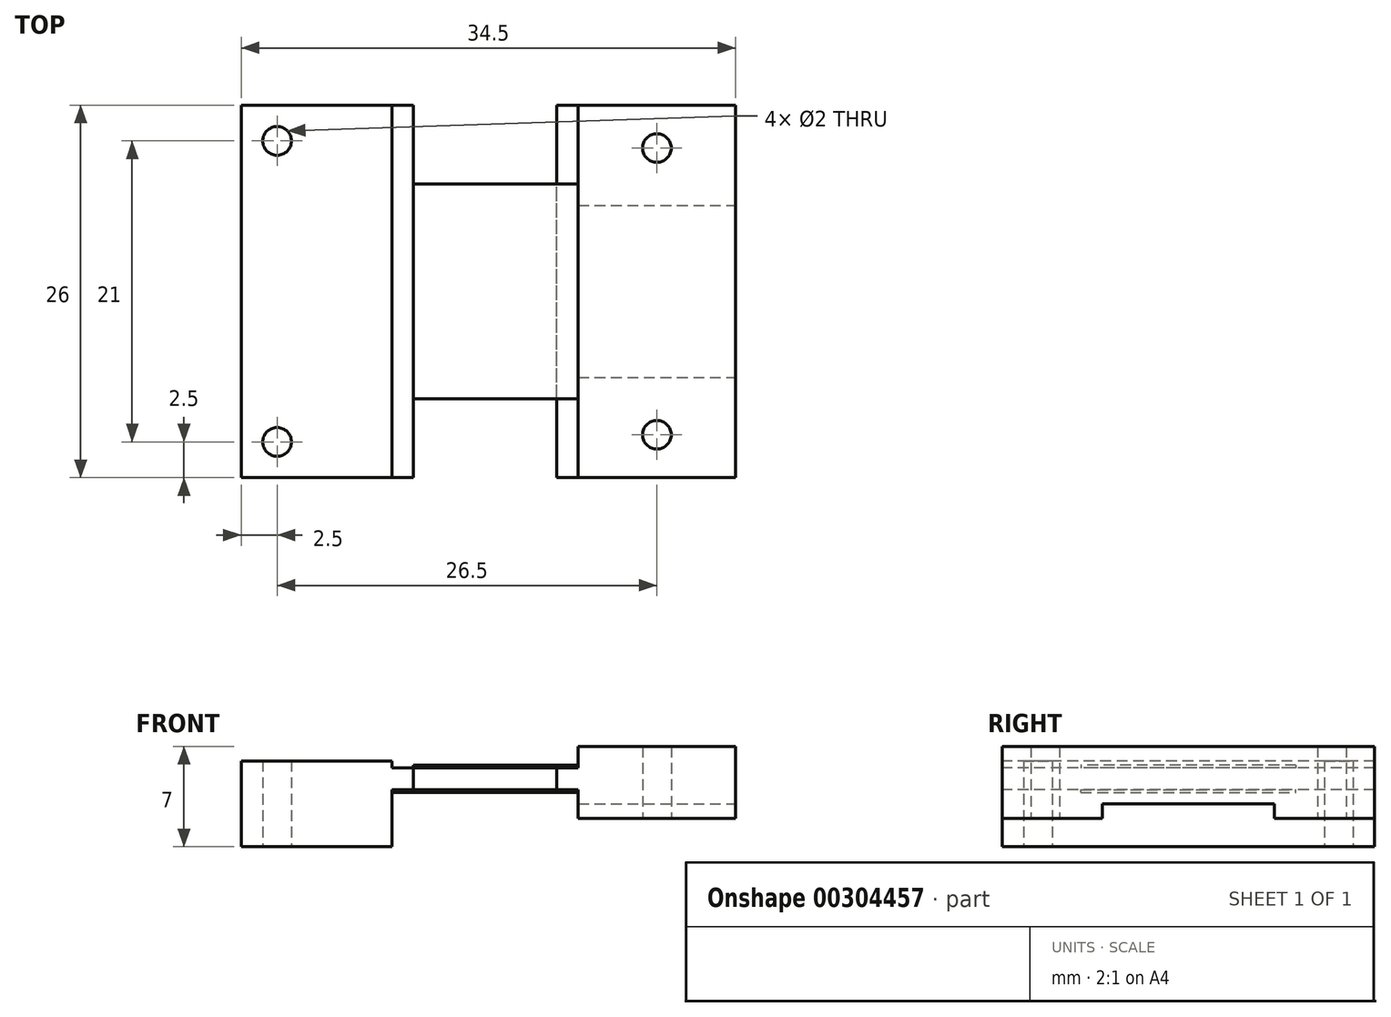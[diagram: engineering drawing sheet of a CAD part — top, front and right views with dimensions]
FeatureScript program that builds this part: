
annotation { "Feature Type Name" : "Feature", "Feature Type Description" : "" }
export const myFeature = defineFeature(function(context is Context, id is Id, definition is map)
    precondition{}
    {
        {
            var Q0;
            Q0=qCreatedBy(makeId("Top.planeOp"),FACE);
            var sketch = newSketch(context, id + "F0", { "sketchPlane" : qUnion([Q0])});
            skLineSegment(sketch, "E0.bottom", {"start": v(6.25, -13) * mm, "end": v(-6.25, -13) * mm});
            skLineSegment(sketch, "E0.top", {"start": v(6.25, 13) * mm, "end": v(-6.25, 13) * mm});
            skLineSegment(sketch, "E0.left", {"start": v(6.25, -13) * mm, "end": v(6.25, 13) * mm});
            skLineSegment(sketch, "E0.right", {"start": v(-6.25, -13) * mm, "end": v(-6.25, 13) * mm});
            skPoint(sketch, "E0.middle", {"position": v(0, 0) * mm});
            skSolve(sketch);
        }
        {
            var Q0;
            Q0 = qSketchRegion(id + "F0", true);
            extrude(context, id + "F1", {"entities" : qUnion([Q0]), "depth" : 5 * mm});
        }
        {
            var Q0;
            Q0=makeQuery(id+"F1.opExtrude","CAP_FACE",FACE,{"disambiguationData":[OSD([sQuery(id+"F0.wireOp",EDGE,"E0.bottom"),sQuery(id+"F0.wireOp",EDGE,"E0.top"),sQuery(id+"F0.wireOp",EDGE,"E0.left"),sQuery(id+"F0.wireOp",EDGE,"E0.right")])],"isStart":false});
            var sketch = newSketch(context, id + "F2", { "sketchPlane" : qUnion([Q0])});
            skLineSegment(sketch, "E1.bottom", {"start": v(-6.25, 13) * mm, "end": v(-4.75, 13) * mm});
            skLineSegment(sketch, "E1.top", {"start": v(-6.25, -13) * mm, "end": v(-4.75, -13) * mm});
            skLineSegment(sketch, "E1.left", {"start": v(-6.25, 13) * mm, "end": v(-6.25, -13) * mm});
            skLineSegment(sketch, "E1.right", {"start": v(-4.75, 13) * mm, "end": v(-4.75, -13) * mm});
            skSolve(sketch);
        }
        {
            var Q0;
            Q0 = qSketchRegion(id + "F2", true);
            extrude(context, id + "F3", {"entities" : qUnion([Q0]), "operationType" : NewBodyOperationType.REMOVE, "oppositeDirection" : true, "depth" : 1.5 * mm});
        }
        {
            var Q0;
            Q0=makeQuery(id+"F1.opExtrude","CAP_FACE",FACE,{"disambiguationData":[OSD([sQuery(id+"F0.wireOp",EDGE,"E0.bottom"),sQuery(id+"F0.wireOp",EDGE,"E0.top"),sQuery(id+"F0.wireOp",EDGE,"E0.left"),sQuery(id+"F0.wireOp",EDGE,"E0.right")])],"isStart":true});
            var sketch = newSketch(context, id + "F4", { "sketchPlane" : qUnion([Q0])});
            skLineSegment(sketch, "E2.bottom", {"start": v(-6.25, 13) * mm, "end": v(-4.75, 13) * mm});
            skLineSegment(sketch, "E2.top", {"start": v(-6.25, -13) * mm, "end": v(-4.75, -13) * mm});
            skLineSegment(sketch, "E2.left", {"start": v(-6.25, 13) * mm, "end": v(-6.25, -13) * mm});
            skLineSegment(sketch, "E2.right", {"start": v(-4.75, 13) * mm, "end": v(-4.75, -13) * mm});
            skSolve(sketch);
        }
        {
            var Q0;
            Q0 = qSketchRegion(id + "F4", true);
            extrude(context, id + "F5", {"entities" : qUnion([Q0]), "operationType" : NewBodyOperationType.REMOVE, "oppositeDirection" : true, "depth" : 2 * mm});
        }
        {
            var Q0;
            Q0=makeQuery(id+"F1.opExtrude","CAP_FACE",FACE,{"disambiguationData":[OSD([sQuery(id+"F0.wireOp",EDGE,"E0.bottom"),sQuery(id+"F0.wireOp",EDGE,"E0.top"),sQuery(id+"F0.wireOp",EDGE,"E0.left"),sQuery(id+"F0.wireOp",EDGE,"E0.right")])],"isStart":true});
            var sketch = newSketch(context, id + "F6", { "sketchPlane" : qUnion([Q0])});
            skLineSegment(sketch, "E3.bottom", {"start": v(-4.75, 6) * mm, "end": v(6.25, 6) * mm});
            skLineSegment(sketch, "E3.top", {"start": v(-4.75, -6) * mm, "end": v(6.25, -6) * mm});
            skLineSegment(sketch, "E3.left", {"start": v(-4.75, 6) * mm, "end": v(-4.75, -6) * mm});
            skLineSegment(sketch, "E3.right", {"start": v(6.25, 6) * mm, "end": v(6.25, -6) * mm});
            skSolve(sketch);
        }
        {
            var Q0;
            Q0 = qSketchRegion(id + "F6", true);
            extrude(context, id + "F7", {"entities" : qUnion([Q0]), "operationType" : NewBodyOperationType.REMOVE, "oppositeDirection" : true, "depth" : 1 * mm});
        }
        {
            var Q0;
            Q0=makeQuery(id+"F1.opExtrude","CAP_FACE",FACE,{"disambiguationData":[OSD([sQuery(id+"F0.wireOp",EDGE,"E0.bottom"),sQuery(id+"F0.wireOp",EDGE,"E0.top"),sQuery(id+"F0.wireOp",EDGE,"E0.left"),sQuery(id+"F0.wireOp",EDGE,"E0.right")])],"isStart":false});
            var sketch = newSketch(context, id + "F8", { "sketchPlane" : qUnion([Q0])});
            skPoint(sketch, "E4", {"position": v(0.75, 10) * mm});
            skPoint(sketch, "E5", {"position": v(0.75, -10) * mm});
            skLineSegment(sketch, "E6", {"start": v(0.75, 16.57) * mm, "end": v(0.75, -16.02) * mm, "construction": true});
            skSolve(sketch);
        }
        {
            var Q0;
            Q0=sQuery(id+"F8.wireOp",VERTEX,"E4");
            var Q1;
            Q1=sQuery(id+"F8.wireOp",VERTEX,"E5");
            var Q2;
            Q2=makeQuery(id+"F1.opExtrude","SWEPT_BODY",BODY,{"disambiguationData":[OSD([sQuery(id+"F0.wireOp",EDGE,"E0.bottom"),sQuery(id+"F0.wireOp",EDGE,"E0.top"),sQuery(id+"F0.wireOp",EDGE,"E0.left"),sQuery(id+"F0.wireOp",EDGE,"E0.right")])]});
            hole(context, id + "F9", {"style" : HoleStyle.SIMPLE, "endStyle" : HoleEndStyle.BLIND, "holeDiameter" : 2 * mm, "holeDepth" : 10 * mm, "isTappedThrough" : true, "tappedDepth" : 12 * mm, "tapClearance" : 3, "locations" : qUnion([Q0, Q1]), "scope" : qUnion([Q2]), "startStyle" : HoleStartStyle.PART});
        }
        {
            var Q0;
            Q0=makeQuery(id+"F3.boolean.opBoolean","COPY",FACE,{"derivedFrom":makeQuery(id+"F3.opExtrude","CAP_FACE",FACE,{"disambiguationData":[OSD([sQuery(id+"F2.wireOp",EDGE,"E1.bottom"),sQuery(id+"F2.wireOp",EDGE,"E1.top"),sQuery(id+"F2.wireOp",EDGE,"E1.left"),sQuery(id+"F2.wireOp",EDGE,"E1.right")])],"isStart":false})});
            var sketch = newSketch(context, id + "F10", { "sketchPlane" : qUnion([Q0])});
            skLineSegment(sketch, "E7.bottom", {"start": v(-4.75, 7.5) * mm, "end": v(-17.75, 7.5) * mm});
            skLineSegment(sketch, "E7.top", {"start": v(-4.75, -7.5) * mm, "end": v(-17.75, -7.5) * mm});
            skLineSegment(sketch, "E7.left", {"start": v(-4.75, 7.5) * mm, "end": v(-4.75, -7.5) * mm});
            skLineSegment(sketch, "E7.right", {"start": v(-17.75, 7.5) * mm, "end": v(-17.75, -7.5) * mm});
            skSolve(sketch);
        }
        {
            var Q0;
            Q0 = qSketchRegion(id + "F10", true);
            extrude(context, id + "F11", {"entities" : qUnion([Q0]), "depth" : 0.2 * mm});
        }
        {
            var Q0;
            Q0=qCreatedBy(makeId("Top.planeOp"),FACE);
            var sketch = newSketch(context, id + "F12", { "sketchPlane" : qUnion([Q0])});
            skLineSegment(sketch, "E8.bottom", {"start": v(-28.25, 13) * mm, "end": v(-16.25, 13) * mm});
            skLineSegment(sketch, "E8.top", {"start": v(-28.25, -13) * mm, "end": v(-16.25, -13) * mm});
            skLineSegment(sketch, "E8.left", {"start": v(-28.25, 13) * mm, "end": v(-28.25, -13) * mm});
            skLineSegment(sketch, "E8.right", {"start": v(-16.25, 13) * mm, "end": v(-16.25, -13) * mm});
            skSolve(sketch);
        }
        {
            var Q0;
            Q0 = qSketchRegion(id + "F12", true);
            extrude(context, id + "F13", {"entities" : qUnion([Q0]), "depth" : 4 * mm, "hasSecondDirection" : true, "secondDirectionOppositeDirection" : true, "secondDirectionDepth" : 2 * mm});
        }
        {
            var Q0;
            Q0=makeQuery(id+"F13.opExtrude","CAP_FACE",FACE,{"disambiguationData":[OSD([sQuery(id+"F12.wireOp",EDGE,"E8.bottom"),sQuery(id+"F12.wireOp",EDGE,"E8.top"),sQuery(id+"F12.wireOp",EDGE,"E8.left"),sQuery(id+"F12.wireOp",EDGE,"E8.right")])],"isStart":false});
            var sketch = newSketch(context, id + "F14", { "sketchPlane" : qUnion([Q0])});
            skLineSegment(sketch, "E9.bottom", {"start": v(-16.25, 13) * mm, "end": v(-17.75, 13) * mm});
            skLineSegment(sketch, "E9.top", {"start": v(-16.25, -13) * mm, "end": v(-17.75, -13) * mm});
            skLineSegment(sketch, "E9.left", {"start": v(-16.25, 13) * mm, "end": v(-16.25, -13) * mm});
            skLineSegment(sketch, "E9.right", {"start": v(-17.75, 13) * mm, "end": v(-17.75, -13) * mm});
            skSolve(sketch);
        }
        {
            var Q0;
            Q0 = qSketchRegion(id + "F14", true);
            extrude(context, id + "F15", {"entities" : qUnion([Q0]), "operationType" : NewBodyOperationType.REMOVE, "oppositeDirection" : true, "depth" : 0.5 * mm});
        }
        {
            var Q0;
            Q0=makeQuery(id+"F13.opExtrude","CAP_FACE",FACE,{"disambiguationData":[OSD([sQuery(id+"F12.wireOp",EDGE,"E8.bottom"),sQuery(id+"F12.wireOp",EDGE,"E8.top"),sQuery(id+"F12.wireOp",EDGE,"E8.left"),sQuery(id+"F12.wireOp",EDGE,"E8.right")])],"isStart":true});
            var sketch = newSketch(context, id + "F16", { "sketchPlane" : qUnion([Q0])});
            skLineSegment(sketch, "E10.bottom", {"start": v(-16.25, 13) * mm, "end": v(-17.75, 13) * mm});
            skLineSegment(sketch, "E10.top", {"start": v(-16.25, -13) * mm, "end": v(-17.75, -13) * mm});
            skLineSegment(sketch, "E10.left", {"start": v(-16.25, 13) * mm, "end": v(-16.25, -13) * mm});
            skLineSegment(sketch, "E10.right", {"start": v(-17.75, 13) * mm, "end": v(-17.75, -13) * mm});
            skSolve(sketch);
        }
        {
            var Q0;
            Q0 = qSketchRegion(id + "F16", true);
            extrude(context, id + "F17", {"entities" : qUnion([Q0]), "operationType" : NewBodyOperationType.REMOVE, "oppositeDirection" : true, "depth" : 4 * mm});
        }
        {
            var Q0;
            Q0=makeQuery(id+"F13.opExtrude","CAP_FACE",FACE,{"disambiguationData":[OSD([sQuery(id+"F12.wireOp",EDGE,"E8.bottom"),sQuery(id+"F12.wireOp",EDGE,"E8.top"),sQuery(id+"F12.wireOp",EDGE,"E8.left"),sQuery(id+"F12.wireOp",EDGE,"E8.right")])],"isStart":false});
            var sketch = newSketch(context, id + "F18", { "sketchPlane" : qUnion([Q0])});
            skLineSegment(sketch, "E11", {"start": v(-25.75, 16.6) * mm, "end": v(-25.75, -18.4) * mm, "construction": true});
            skPoint(sketch, "E12", {"position": v(-25.75, 10.5) * mm});
            skPoint(sketch, "E13", {"position": v(-25.75, -10.5) * mm});
            skSolve(sketch);
        }
        {
            var Q0;
            Q0=sQuery(id+"F18.wireOp",VERTEX,"E12");
            var Q1;
            Q1=sQuery(id+"F18.wireOp",VERTEX,"E13");
            var Q2;
            Q2=makeQuery(id+"F13.opExtrude","SWEPT_BODY",BODY,{"disambiguationData":[OSD([sQuery(id+"F12.wireOp",EDGE,"E8.bottom"),sQuery(id+"F12.wireOp",EDGE,"E8.top"),sQuery(id+"F12.wireOp",EDGE,"E8.left"),sQuery(id+"F12.wireOp",EDGE,"E8.right")])]});
            hole(context, id + "F19", {"style" : HoleStyle.SIMPLE, "endStyle" : HoleEndStyle.BLIND, "holeDiameter" : 2 * mm, "holeDepth" : 10 * mm, "isTappedThrough" : true, "tappedDepth" : 12 * mm, "tapClearance" : 3, "locations" : qUnion([Q0, Q1]), "scope" : qUnion([Q2]), "startStyle" : HoleStartStyle.PART});
        }
        {
            var Q0;
            Q0=makeQuery(id+"F17.boolean.opBoolean","COPY",FACE,{"derivedFrom":makeQuery(id+"F17.opExtrude","CAP_FACE",FACE,{"disambiguationData":[OSD([sQuery(id+"F16.wireOp",EDGE,"E10.bottom"),sQuery(id+"F16.wireOp",EDGE,"E10.top"),sQuery(id+"F16.wireOp",EDGE,"E10.left"),sQuery(id+"F16.wireOp",EDGE,"E10.right")])],"isStart":false})});
            var sketch = newSketch(context, id + "F20", { "sketchPlane" : qUnion([Q0])});
            skLineSegment(sketch, "E14.bottom", {"start": v(-17.75, 7.5) * mm, "end": v(-4.75, 7.5) * mm});
            skLineSegment(sketch, "E14.top", {"start": v(-17.75, -7.5) * mm, "end": v(-4.75, -7.5) * mm});
            skLineSegment(sketch, "E14.left", {"start": v(-17.75, 7.5) * mm, "end": v(-17.75, -7.5) * mm});
            skLineSegment(sketch, "E14.right", {"start": v(-4.75, 7.5) * mm, "end": v(-4.75, -7.5) * mm});
            skSolve(sketch);
        }
        {
            var Q0;
            Q0 = qSketchRegion(id + "F20", true);
            extrude(context, id + "F21", {"entities" : qUnion([Q0]), "depth" : 0.2 * mm});
        }
    });
